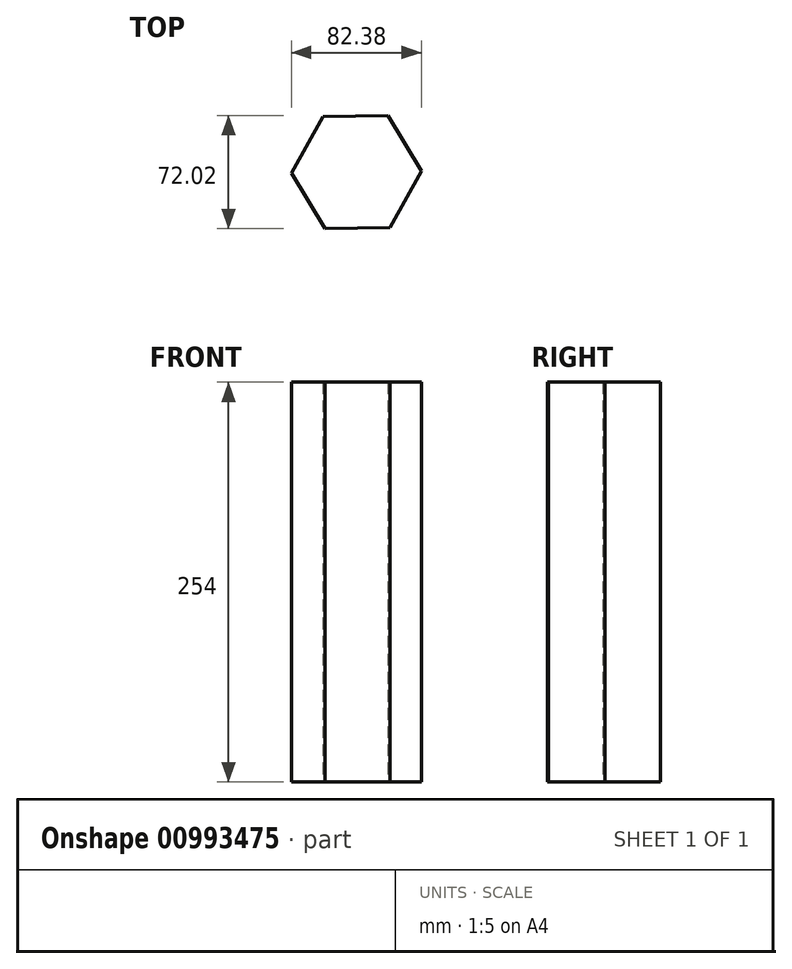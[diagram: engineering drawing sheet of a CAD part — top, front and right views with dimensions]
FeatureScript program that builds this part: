
annotation { "Feature Type Name" : "Feature", "Feature Type Description" : "" }
export const myFeature = defineFeature(function(context is Context, id is Id, definition is map)
    precondition{}
    {
        {
            var Q0;
            Q0=qCreatedBy(makeId("Top.planeOp"),FACE);
            var sketch = newSketch(context, id + "F0", { "sketchPlane" : qUnion([Q0])});
            skCircle(sketch, "E0.cCircle", {"center": v(0, 0) * mm, "radius": 35.68 * mm, "construction": true});
            skLineSegment(sketch, "E0.0", {"start": v(-41.2, -0.68) * mm, "end": v(-21.18, 35.33) * mm});
            skLineSegment(sketch, "E0.1", {"start": v(-21.18, 35.33) * mm, "end": v(20, 36.01) * mm});
            skLineSegment(sketch, "E0.2", {"start": v(20, 36.01) * mm, "end": v(41.2, 0.68) * mm});
            skLineSegment(sketch, "E0.3", {"start": v(41.2, 0.68) * mm, "end": v(21.18, -35.33) * mm});
            skLineSegment(sketch, "E0.4", {"start": v(21.18, -35.33) * mm, "end": v(-20, -36.01) * mm});
            skLineSegment(sketch, "E0.5", {"start": v(-20, -36.01) * mm, "end": v(-41.2, -0.68) * mm});
            skPoint(sketch, "E0.0.midPoint", {"position": v(-31.19, 17.33) * mm});
            skSolve(sketch);
        }
        {
            var Q0;
            Q0=makeQuery(id+"F0.imprint","IMPRINT",FACE,{"disambiguationData":[TD([[makeQuery(id+"F0.imprint","IMPRINT",EDGE,{"derivedFrom":sQuery(id+"F0.wireOp",EDGE,"E0.0")}),-1.0]])]});
            extrude(context, id + "F1", {"entities" : qUnion([Q0]), "depth" : 254 * mm, "offsetDistance" : 25.4 * mm});
        }
        {
            var Q0;
            Q0=makeQuery(id+"F1.opExtrude","CAP_FACE",FACE,{"disambiguationData":[OSD([sQuery(id+"F0.wireOp",EDGE,"E0.0"),sQuery(id+"F0.wireOp",EDGE,"E0.1"),sQuery(id+"F0.wireOp",EDGE,"E0.2"),sQuery(id+"F0.wireOp",EDGE,"E0.3"),sQuery(id+"F0.wireOp",EDGE,"E0.4"),sQuery(id+"F0.wireOp",EDGE,"E0.5")])],"isStart":false});
            var sketch = newSketch(context, id + "F2", { "sketchPlane" : qUnion([Q0])});
            skCircle(sketch, "E1", {"center": v(0, 0) * mm, "radius": 23.52 * mm});
            skSolve(sketch);
        }
        {
            var Q0;
            Q0=makeQuery(id+"F2.imprint","IMPRINT",FACE,{"disambiguationData":[TD([[makeQuery(id+"F2.imprint","IMPRINT",EDGE,{"derivedFrom":sQuery(id+"F2.wireOp",EDGE,"E1")}),1.0]])]});
            extrude(context, id + "F3", {"entities" : qUnion([Q0]), "operationType" : NewBodyOperationType.ADD, "oppositeDirection" : true, "depth" : 111.76 * mm, "offsetDistance" : 25.4 * mm});
        }
    });
